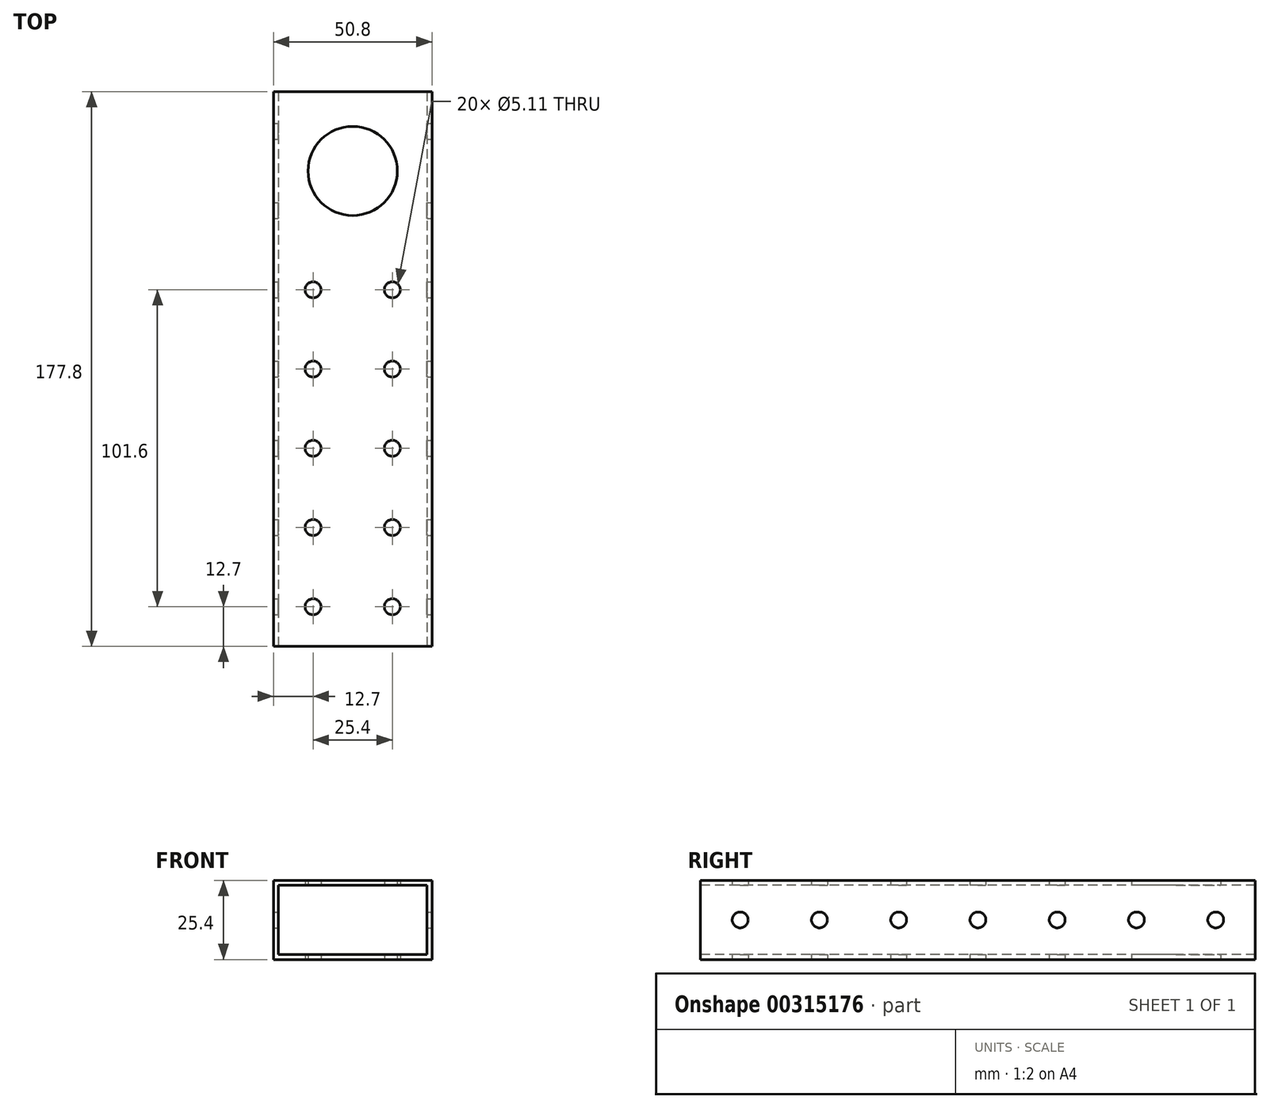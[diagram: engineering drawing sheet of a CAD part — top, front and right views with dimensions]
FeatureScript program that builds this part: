
annotation { "Feature Type Name" : "Feature", "Feature Type Description" : "" }
export const myFeature = defineFeature(function(context is Context, id is Id, definition is map)
    precondition{}
    {
        {
            var Q0;
            Q0=qCreatedBy(makeId("Front.planeOp"),FACE);
            var sketch = newSketch(context, id + "F0", { "sketchPlane" : qUnion([Q0])});
            skLineSegment(sketch, "E0.bottom", {"start": v(25.4, -12.7) * mm, "end": v(-25.4, -12.7) * mm});
            skLineSegment(sketch, "E0.top", {"start": v(25.4, 12.7) * mm, "end": v(-25.4, 12.7) * mm});
            skLineSegment(sketch, "E0.left", {"start": v(25.4, -12.7) * mm, "end": v(25.4, 12.7) * mm});
            skLineSegment(sketch, "E0.right", {"start": v(-25.4, -12.7) * mm, "end": v(-25.4, 12.7) * mm});
            skPoint(sketch, "E0.middle", {"position": v(0, 0) * mm});
            skSolve(sketch);
        }
        {
            var Q0;
            Q0 = qSketchRegion(id + "F0", true);
            extrude(context, id + "F1", {"entities" : qUnion([Q0]), "depth" : 177.8 * mm});
        }
        {
            var Q0;
            Q0=makeQuery(id+"F1.opExtrude","SWEPT_FACE",FACE,{"disambiguationData":[OSD([sQuery(id+"F0.wireOp",EDGE,"E0.left")])]});
            var sketch = newSketch(context, id + "F2", { "sketchPlane" : qUnion([Q0])});
            skCircle(sketch, "E1", {"center": v(-165.1, 0) * mm, "radius": 2.55 * mm});
            skCircle(sketch, "E2.1.0.0", {"center": v(-139.7, 0) * mm, "radius": 2.55 * mm});
            skCircle(sketch, "E2.2.0.0", {"center": v(-114.3, 0) * mm, "radius": 2.55 * mm});
            skCircle(sketch, "E2.3.0.0", {"center": v(-88.9, 0) * mm, "radius": 2.55 * mm});
            skCircle(sketch, "E2.4.0.0", {"center": v(-63.5, 0) * mm, "radius": 2.55 * mm});
            skCircle(sketch, "E2.5.0.0", {"center": v(-38.1, 0) * mm, "radius": 2.55 * mm});
            skCircle(sketch, "E2.6.0.0", {"center": v(-12.7, 0) * mm, "radius": 2.55 * mm});
            skCircle(sketch, "E2.7.0.0", {"center": v(12.7, 0) * mm, "radius": 2.55 * mm});
            skLineSegment(sketch, "E2.direction1", {"start": v(-165.1, 0) * mm, "end": v(-139.7, 0) * mm, "construction": true});
            skSolve(sketch);
        }
        {
            var Q0;
            Q0=makeQuery(id+"F1.opExtrude","CAP_FACE",FACE,{"disambiguationData":[OSD([sQuery(id+"F0.wireOp",EDGE,"E0.bottom"),sQuery(id+"F0.wireOp",EDGE,"E0.top"),sQuery(id+"F0.wireOp",EDGE,"E0.left"),sQuery(id+"F0.wireOp",EDGE,"E0.right")])],"isStart":false});
            var sketch = newSketch(context, id + "F3", { "sketchPlane" : qUnion([Q0])});
            skLineSegment(sketch, "E3.bottom", {"start": v(23.81, -11.11) * mm, "end": v(-23.81, -11.11) * mm});
            skLineSegment(sketch, "E3.top", {"start": v(23.81, 11.11) * mm, "end": v(-23.81, 11.11) * mm});
            skLineSegment(sketch, "E3.left", {"start": v(23.81, -11.11) * mm, "end": v(23.81, 11.11) * mm});
            skLineSegment(sketch, "E3.right", {"start": v(-23.81, -11.11) * mm, "end": v(-23.81, 11.11) * mm});
            skPoint(sketch, "E3.middle", {"position": v(0, 0) * mm});
            skSolve(sketch);
        }
        {
            var Q0;
            Q0 = qSketchRegion(id + "F3", true);
            extrude(context, id + "F4", {"entities" : qUnion([Q0]), "operationType" : NewBodyOperationType.REMOVE, "oppositeDirection" : true, "depth" : 203.2 * mm});
        }
        {
            var Q0;
            Q0=makeQuery(id+"F2.imprint","IMPRINT",FACE,{"disambiguationData":[TD([[makeQuery(id+"F2.imprint","IMPRINT",EDGE,{"derivedFrom":sQuery(id+"F2.wireOp",EDGE,"E1")}),1.0]])]});
            var Q1;
            Q1=makeQuery(id+"F2.imprint","IMPRINT",FACE,{"disambiguationData":[TD([[makeQuery(id+"F2.imprint","IMPRINT",EDGE,{"derivedFrom":sQuery(id+"F2.wireOp",EDGE,"E2.1.0.0")}),1.0]])]});
            var Q2;
            Q2=makeQuery(id+"F2.imprint","IMPRINT",FACE,{"disambiguationData":[TD([[makeQuery(id+"F2.imprint","IMPRINT",EDGE,{"derivedFrom":sQuery(id+"F2.wireOp",EDGE,"E2.2.0.0")}),1.0]])]});
            var Q3;
            Q3=makeQuery(id+"F2.imprint","IMPRINT",FACE,{"disambiguationData":[TD([[makeQuery(id+"F2.imprint","IMPRINT",EDGE,{"derivedFrom":sQuery(id+"F2.wireOp",EDGE,"E2.3.0.0")}),1.0]])]});
            var Q4;
            Q4=makeQuery(id+"F2.imprint","IMPRINT",FACE,{"disambiguationData":[TD([[makeQuery(id+"F2.imprint","IMPRINT",EDGE,{"derivedFrom":sQuery(id+"F2.wireOp",EDGE,"E2.4.0.0")}),1.0]])]});
            var Q5;
            Q5=makeQuery(id+"F2.imprint","IMPRINT",FACE,{"disambiguationData":[TD([[makeQuery(id+"F2.imprint","IMPRINT",EDGE,{"derivedFrom":sQuery(id+"F2.wireOp",EDGE,"E2.5.0.0")}),1.0]])]});
            var Q6;
            Q6=makeQuery(id+"F2.imprint","IMPRINT",FACE,{"disambiguationData":[TD([[makeQuery(id+"F2.imprint","IMPRINT",EDGE,{"derivedFrom":sQuery(id+"F2.wireOp",EDGE,"E2.6.0.0")}),1.0]])]});
            var Q7;
            Q7=makeQuery(id+"F2.imprint","IMPRINT",FACE,{"disambiguationData":[TD([[makeQuery(id+"F2.imprint","IMPRINT",EDGE,{"derivedFrom":sQuery(id+"F2.wireOp",EDGE,"E2.7.0.0")}),1.0]])]});
            var Q8;
            Q8=sQuery(id+"F2.wireOp",EDGE,"E1");
            var Q9;
            Q9=sQuery(id+"F2.wireOp",EDGE,"E2.1.0.0");
            var Q10;
            Q10=sQuery(id+"F2.wireOp",EDGE,"E2.2.0.0");
            var Q11;
            Q11=sQuery(id+"F2.wireOp",EDGE,"E2.3.0.0");
            var Q12;
            Q12=sQuery(id+"F2.wireOp",EDGE,"E2.4.0.0");
            var Q13;
            Q13=sQuery(id+"F2.wireOp",EDGE,"E2.5.0.0");
            var Q14;
            Q14=sQuery(id+"F2.wireOp",EDGE,"E2.6.0.0");
            var Q15;
            Q15=sQuery(id+"F2.wireOp",EDGE,"E2.7.0.0");
            extrude(context, id + "F5", {"entities" : qUnion([Q0, Q1, Q2, Q3, Q4, Q5, Q6, Q7]), "operationType" : NewBodyOperationType.REMOVE, "surfaceEntities" : qUnion([Q8, Q9, Q10, Q11, Q12, Q13, Q14, Q15]), "oppositeDirection" : true, "depth" : 76.2 * mm});
        }
        {
            var Q0;
            Q0=makeQuery(id+"F1.opExtrude","SWEPT_FACE",FACE,{"disambiguationData":[OSD([sQuery(id+"F0.wireOp",EDGE,"E0.bottom")])]});
            var sketch = newSketch(context, id + "F6", { "sketchPlane" : qUnion([Q0])});
            skCircle(sketch, "E4", {"center": v(12.7, 165.1) * mm, "radius": 2.55 * mm});
            skCircle(sketch, "E5.1.0.0", {"center": v(12.7, 139.7) * mm, "radius": 2.55 * mm});
            skCircle(sketch, "E5.2.0.0", {"center": v(12.7, 114.3) * mm, "radius": 2.55 * mm});
            skCircle(sketch, "E5.3.0.0", {"center": v(12.7, 88.9) * mm, "radius": 2.55 * mm});
            skCircle(sketch, "E5.4.0.0", {"center": v(12.7, 63.5) * mm, "radius": 2.55 * mm});
            skLineSegment(sketch, "E5.direction1", {"start": v(12.7, 165.1) * mm, "end": v(12.7, 139.7) * mm, "construction": true});
            skCircle(sketch, "E6", {"center": v(-12.7, 165.1) * mm, "radius": 2.55 * mm});
            skCircle(sketch, "E7.0.1.0", {"center": v(-12.7, 139.7) * mm, "radius": 2.55 * mm});
            skCircle(sketch, "E7.0.2.0", {"center": v(-12.7, 114.3) * mm, "radius": 2.55 * mm});
            skCircle(sketch, "E7.0.3.0", {"center": v(-12.7, 88.9) * mm, "radius": 2.55 * mm});
            skCircle(sketch, "E7.0.4.0", {"center": v(-12.7, 63.5) * mm, "radius": 2.55 * mm});
            skLineSegment(sketch, "E7.direction1", {"start": v(-12.7, 165.1) * mm, "end": v(-0.25, 165.1) * mm, "construction": true});
            skLineSegment(sketch, "E7.direction2", {"start": v(-12.7, 165.1) * mm, "end": v(-12.7, 139.7) * mm, "construction": true});
            skLineSegment(sketch, "E8.direction1", {"start": v(-0.25, 165.1) * mm, "end": v(26.42, 167.13) * mm, "construction": true});
            skLineSegment(sketch, "E8.direction2", {"start": v(-0.25, 165.1) * mm, "end": v(-0.5, 139.7) * mm, "construction": true});
            skCircle(sketch, "E9", {"center": v(0, 25.4) * mm, "radius": 14.29 * mm});
            skSolve(sketch);
        }
        {
            var Q0;
            Q0=makeQuery(id+"F6.imprint","IMPRINT",FACE,{"disambiguationData":[TD([[makeQuery(id+"F6.imprint","IMPRINT",EDGE,{"derivedFrom":sQuery(id+"F6.wireOp",EDGE,"E6")}),1.0]])]});
            var Q1;
            Q1=makeQuery(id+"F6.imprint","IMPRINT",FACE,{"disambiguationData":[TD([[makeQuery(id+"F6.imprint","IMPRINT",EDGE,{"derivedFrom":sQuery(id+"F6.wireOp",EDGE,"E7.0.1.0")}),1.0]])]});
            var Q2;
            Q2=makeQuery(id+"F6.imprint","IMPRINT",FACE,{"disambiguationData":[TD([[makeQuery(id+"F6.imprint","IMPRINT",EDGE,{"derivedFrom":sQuery(id+"F6.wireOp",EDGE,"E7.0.2.0")}),1.0]])]});
            var Q3;
            Q3=makeQuery(id+"F6.imprint","IMPRINT",FACE,{"disambiguationData":[TD([[makeQuery(id+"F6.imprint","IMPRINT",EDGE,{"derivedFrom":sQuery(id+"F6.wireOp",EDGE,"E7.0.3.0")}),1.0]])]});
            var Q4;
            Q4=makeQuery(id+"F6.imprint","IMPRINT",FACE,{"disambiguationData":[TD([[makeQuery(id+"F6.imprint","IMPRINT",EDGE,{"derivedFrom":sQuery(id+"F6.wireOp",EDGE,"E7.0.4.0")}),1.0]])]});
            var Q5;
            Q5=makeQuery(id+"F6.imprint","IMPRINT",FACE,{"disambiguationData":[TD([[makeQuery(id+"F6.imprint","IMPRINT",EDGE,{"derivedFrom":sQuery(id+"F6.wireOp",EDGE,"E7.0.5.0")}),1.0]])]});
            var Q6;
            Q6=makeQuery(id+"F6.imprint","IMPRINT",FACE,{"disambiguationData":[TD([[makeQuery(id+"F6.imprint","IMPRINT",EDGE,{"derivedFrom":sQuery(id+"F6.wireOp",EDGE,"E7.0.6.0")}),1.0]])]});
            var Q7;
            Q7=makeQuery(id+"F6.imprint","IMPRINT",FACE,{"disambiguationData":[TD([[makeQuery(id+"F6.imprint","IMPRINT",EDGE,{"derivedFrom":sQuery(id+"F6.wireOp",EDGE,"E7.0.7.0")}),1.0]])]});
            var Q8;
            Q8=makeQuery(id+"F6.imprint","IMPRINT",FACE,{"disambiguationData":[TD([[makeQuery(id+"F6.imprint","IMPRINT",EDGE,{"derivedFrom":sQuery(id+"F6.wireOp",EDGE,"E5.7.0.0")}),1.0]])]});
            var Q9;
            Q9=makeQuery(id+"F6.imprint","IMPRINT",FACE,{"disambiguationData":[TD([[makeQuery(id+"F6.imprint","IMPRINT",EDGE,{"derivedFrom":sQuery(id+"F6.wireOp",EDGE,"E5.6.0.0")}),1.0]])]});
            var Q10;
            Q10=makeQuery(id+"F6.imprint","IMPRINT",FACE,{"disambiguationData":[TD([[makeQuery(id+"F6.imprint","IMPRINT",EDGE,{"derivedFrom":sQuery(id+"F6.wireOp",EDGE,"E5.5.0.0")}),1.0]])]});
            var Q11;
            Q11=makeQuery(id+"F6.imprint","IMPRINT",FACE,{"disambiguationData":[TD([[makeQuery(id+"F6.imprint","IMPRINT",EDGE,{"derivedFrom":sQuery(id+"F6.wireOp",EDGE,"E5.4.0.0")}),1.0]])]});
            var Q12;
            Q12=makeQuery(id+"F6.imprint","IMPRINT",FACE,{"disambiguationData":[TD([[makeQuery(id+"F6.imprint","IMPRINT",EDGE,{"derivedFrom":sQuery(id+"F6.wireOp",EDGE,"E5.3.0.0")}),1.0]])]});
            var Q13;
            Q13=makeQuery(id+"F6.imprint","IMPRINT",FACE,{"disambiguationData":[TD([[makeQuery(id+"F6.imprint","IMPRINT",EDGE,{"derivedFrom":sQuery(id+"F6.wireOp",EDGE,"E5.2.0.0")}),1.0]])]});
            var Q14;
            Q14=makeQuery(id+"F6.imprint","IMPRINT",FACE,{"disambiguationData":[TD([[makeQuery(id+"F6.imprint","IMPRINT",EDGE,{"derivedFrom":sQuery(id+"F6.wireOp",EDGE,"E5.1.0.0")}),1.0]])]});
            var Q15;
            Q15=makeQuery(id+"F6.imprint","IMPRINT",FACE,{"disambiguationData":[TD([[makeQuery(id+"F6.imprint","IMPRINT",EDGE,{"derivedFrom":sQuery(id+"F6.wireOp",EDGE,"E4")}),1.0]])]});
            var Q16;
            Q16=makeQuery(id+"F6.imprint","IMPRINT",FACE,{"disambiguationData":[TD([[makeQuery(id+"F6.imprint","IMPRINT",EDGE,{"derivedFrom":sQuery(id+"F6.wireOp",EDGE,"Vj9fxD2r-8x7n-ITew-BgU5-dIDONOYKnPN6")}),1.0]])]});
            var Q17;
            Q17=makeQuery(id+"F6.imprint","IMPRINT",FACE,{"disambiguationData":[TD([[makeQuery(id+"F6.imprint","IMPRINT",EDGE,{"derivedFrom":sQuery(id+"F6.wireOp",EDGE,"E8.0.1.0")}),1.0]])]});
            var Q18;
            Q18=makeQuery(id+"F6.imprint","IMPRINT",FACE,{"disambiguationData":[TD([[makeQuery(id+"F6.imprint","IMPRINT",EDGE,{"derivedFrom":sQuery(id+"F6.wireOp",EDGE,"E8.0.2.0")}),1.0]])]});
            var Q19;
            Q19=makeQuery(id+"F6.imprint","IMPRINT",FACE,{"disambiguationData":[TD([[makeQuery(id+"F6.imprint","IMPRINT",EDGE,{"derivedFrom":sQuery(id+"F6.wireOp",EDGE,"E8.0.3.0")}),1.0]])]});
            var Q20;
            Q20=makeQuery(id+"F6.imprint","IMPRINT",FACE,{"disambiguationData":[TD([[makeQuery(id+"F6.imprint","IMPRINT",EDGE,{"derivedFrom":sQuery(id+"F6.wireOp",EDGE,"E8.0.4.0")}),1.0]])]});
            var Q21;
            Q21=makeQuery(id+"F6.imprint","IMPRINT",FACE,{"disambiguationData":[TD([[makeQuery(id+"F6.imprint","IMPRINT",EDGE,{"derivedFrom":sQuery(id+"F6.wireOp",EDGE,"E8.0.5.0")}),1.0]])]});
            var Q22;
            Q22=makeQuery(id+"F6.imprint","IMPRINT",FACE,{"disambiguationData":[TD([[makeQuery(id+"F6.imprint","IMPRINT",EDGE,{"derivedFrom":sQuery(id+"F6.wireOp",EDGE,"E8.0.6.0")}),1.0]])]});
            var Q23;
            Q23=makeQuery(id+"F6.imprint","IMPRINT",FACE,{"disambiguationData":[TD([[makeQuery(id+"F6.imprint","IMPRINT",EDGE,{"derivedFrom":sQuery(id+"F6.wireOp",EDGE,"E8.0.7.0")}),1.0]])]});
            var Q24;
            Q24=sQuery(id+"F6.wireOp",EDGE,"E4");
            var Q25;
            Q25=sQuery(id+"F6.wireOp",EDGE,"E5.1.0.0");
            var Q26;
            Q26=sQuery(id+"F6.wireOp",EDGE,"E5.2.0.0");
            var Q27;
            Q27=sQuery(id+"F6.wireOp",EDGE,"E5.3.0.0");
            var Q28;
            Q28=sQuery(id+"F6.wireOp",EDGE,"E5.4.0.0");
            var Q29;
            Q29=sQuery(id+"F6.wireOp",EDGE,"E5.5.0.0");
            var Q30;
            Q30=sQuery(id+"F6.wireOp",EDGE,"E5.6.0.0");
            var Q31;
            Q31=sQuery(id+"F6.wireOp",EDGE,"E5.7.0.0");
            var Q32;
            Q32=sQuery(id+"F6.wireOp",EDGE,"E7.0.7.0");
            var Q33;
            Q33=sQuery(id+"F6.wireOp",EDGE,"E7.0.6.0");
            var Q34;
            Q34=sQuery(id+"F6.wireOp",EDGE,"E7.0.5.0");
            var Q35;
            Q35=sQuery(id+"F6.wireOp",EDGE,"E7.0.4.0");
            var Q36;
            Q36=sQuery(id+"F6.wireOp",EDGE,"E7.0.3.0");
            var Q37;
            Q37=sQuery(id+"F6.wireOp",EDGE,"E7.0.2.0");
            var Q38;
            Q38=sQuery(id+"F6.wireOp",EDGE,"E7.0.1.0");
            var Q39;
            Q39=sQuery(id+"F6.wireOp",EDGE,"E6");
            extrude(context, id + "F7", {"entities" : qUnion([Q0, Q1, Q2, Q3, Q4, Q5, Q6, Q7, Q8, Q9, Q10, Q11, Q12, Q13, Q14, Q15, Q16, Q17, Q18, Q19, Q20, Q21, Q22, Q23]), "operationType" : NewBodyOperationType.REMOVE, "surfaceEntities" : qUnion([Q24, Q25, Q26, Q27, Q28, Q29, Q30, Q31, Q32, Q33, Q34, Q35, Q36, Q37, Q38, Q39]), "oppositeDirection" : true, "depth" : 50.8 * mm});
        }
        {
            var Q0;
            Q0=makeQuery(id+"F6.imprint","IMPRINT",FACE,{"disambiguationData":[TD([[makeQuery(id+"F6.imprint","IMPRINT",EDGE,{"derivedFrom":sQuery(id+"F6.wireOp",EDGE,"E9")}),1.0]])]});
            extrude(context, id + "F8", {"entities" : qUnion([Q0]), "operationType" : NewBodyOperationType.REMOVE, "oppositeDirection" : true, "depth" : 50.8 * mm});
        }
    });
